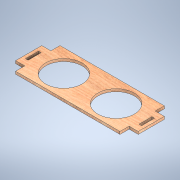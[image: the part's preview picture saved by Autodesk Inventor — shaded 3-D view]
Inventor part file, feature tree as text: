
AUTODESK INVENTOR PART (.ipt)
format: ipt  version: 2022 (Build 260153000, 153)  size: 171,520 bytes
history: native  units: mm
features: extrude x4, sketch x4, other x1
ambient origin geometry x8: Origin, YZ Plane, XZ Plane, XY Plane, X Axis, Y Axis, Z Axis, Center Point
bodies: Body1 (feature_tree)
feature tree (9):
  other  "Sólido1"
  extrude  "Extrusión1"  Depth=170.0mm
  extrude  "Extrusión2"  TaperAngle=0.0deg  [1 undecoded]
  extrude  "Extrusión3"  TaperAngle=180.0deg  [1 undecoded]
  extrude  "Extrusión4"  Depth=10.0mm TaperAngle=0.0deg
  sketch  "Boceto1"  dims[d0=400.0mm d1=170.0mm]
  sketch  "Boceto2"  dims[d2=10.0mm d3=0.0mm]
  sketch  "Boceto3"  dims[d5=100.0mm d6=180.0deg]
  sketch  "Boceto4"  dims[d7=140.0mm d8=10.0mm d9=0.0mm d10=70.0mm d11=100.0mm d12=10.0mm d13=0.0mm d14=17.5mm d15=0.0mm d16=10.0mm d17=50.0mm d18=10.0mm d19=0.0mm]
note: 2 required parameter values undecoded (feature->parameter linkage not recoverable at this tier; creation-order binding heuristic only, values carry confidence <= 0.55)
